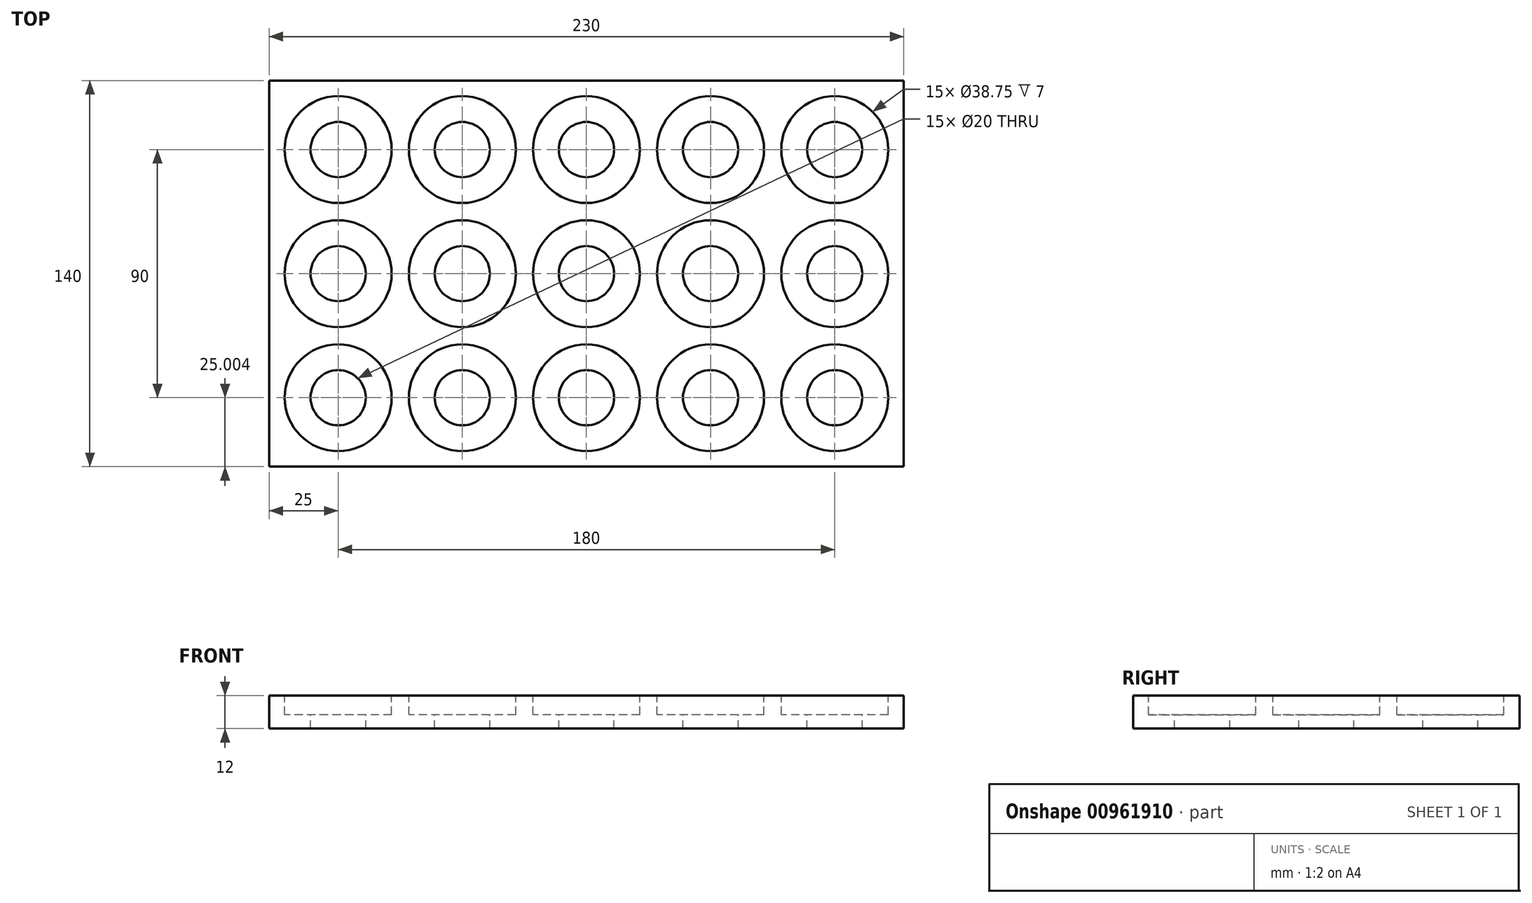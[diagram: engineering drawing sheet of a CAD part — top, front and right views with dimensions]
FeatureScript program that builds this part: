
annotation { "Feature Type Name" : "Feature", "Feature Type Description" : "" }
export const myFeature = defineFeature(function(context is Context, id is Id, definition is map)
    precondition{}
    {
        {
            var Q0;
            Q0=qCreatedBy(makeId("Top.planeOp"),FACE);
            var sketch = newSketch(context, id + "F0", { "sketchPlane" : qUnion([Q0])});
            skLineSegment(sketch, "E0.bottom", {"start": v(-57.94, 101.27) * mm, "end": v(172.06, 101.27) * mm});
            skLineSegment(sketch, "E0.top", {"start": v(-57.94, -38.73) * mm, "end": v(172.06, -38.73) * mm});
            skLineSegment(sketch, "E0.left", {"start": v(-57.94, 101.27) * mm, "end": v(-57.94, -38.73) * mm});
            skLineSegment(sketch, "E0.right", {"start": v(172.06, 101.27) * mm, "end": v(172.06, -38.73) * mm});
            skSolve(sketch);
        }
        {
            var Q0;
            Q0=qSketchRegion(id+"F0",true);
            extrude(context, id + "F1", {"entities" : qUnion([Q0]), "depth" : 12 * mm, "offsetDistance" : 25 * mm});
        }
        {
            var Q0;
            Q0=makeQuery(id+"F1.opExtrude","CAP_FACE",FACE,{"disambiguationData":[OSD([sQuery(id+"F0.wireOp",EDGE,"E0.bottom"),sQuery(id+"F0.wireOp",EDGE,"E0.top"),sQuery(id+"F0.wireOp",EDGE,"E0.left"),sQuery(id+"F0.wireOp",EDGE,"E0.right")])],"isStart":false});
            var sketch = newSketch(context, id + "F2", { "sketchPlane" : qUnion([Q0])});
            skCircle(sketch, "E1", {"center": v(-32.94, 76.27) * mm, "radius": 19.38 * mm});
            skCircle(sketch, "E2", {"center": v(-32.94, 31.27) * mm, "radius": 19.38 * mm});
            skPoint(sketch, "E2.centerSnap0", {"position": v(-57.94, 31.27) * mm});
            skCircle(sketch, "E3", {"center": v(-32.94, -13.73) * mm, "radius": 19.38 * mm});
            skCircle(sketch, "E4", {"center": v(12.06, 76.27) * mm, "radius": 19.38 * mm});
            skCircle(sketch, "E5", {"center": v(12.06, 31.27) * mm, "radius": 19.38 * mm});
            skCircle(sketch, "E6", {"center": v(12.06, -13.73) * mm, "radius": 19.38 * mm});
            skCircle(sketch, "E7", {"center": v(57.06, 76.27) * mm, "radius": 19.38 * mm});
            skCircle(sketch, "E8", {"center": v(57.06, 31.27) * mm, "radius": 19.38 * mm});
            skCircle(sketch, "E9", {"center": v(57.06, -13.73) * mm, "radius": 19.38 * mm});
            skCircle(sketch, "E10", {"center": v(102.06, 76.27) * mm, "radius": 19.38 * mm});
            skCircle(sketch, "E11", {"center": v(102.06, 31.27) * mm, "radius": 19.38 * mm});
            skCircle(sketch, "E12", {"center": v(102.06, -13.73) * mm, "radius": 19.38 * mm});
            skCircle(sketch, "E13", {"center": v(147.06, 76.27) * mm, "radius": 19.38 * mm});
            skCircle(sketch, "E14", {"center": v(147.06, 31.27) * mm, "radius": 19.38 * mm});
            skCircle(sketch, "E15", {"center": v(147.06, -13.73) * mm, "radius": 19.38 * mm});
            skCircle(sketch, "E16", {"center": v(-32.94, 76.27) * mm, "radius": 10 * mm});
            skCircle(sketch, "E17", {"center": v(-32.94, 31.27) * mm, "radius": 10 * mm});
            skCircle(sketch, "E18", {"center": v(-32.94, -13.73) * mm, "radius": 10 * mm});
            skCircle(sketch, "E19", {"center": v(12.06, -13.73) * mm, "radius": 10 * mm});
            skCircle(sketch, "E20", {"center": v(12.06, 31.27) * mm, "radius": 10 * mm});
            skCircle(sketch, "E21", {"center": v(12.06, 76.27) * mm, "radius": 10 * mm});
            skCircle(sketch, "E22", {"center": v(57.06, 76.27) * mm, "radius": 10 * mm});
            skCircle(sketch, "E23", {"center": v(57.06, 31.27) * mm, "radius": 10 * mm});
            skCircle(sketch, "E24", {"center": v(57.06, -13.73) * mm, "radius": 10 * mm});
            skCircle(sketch, "E25", {"center": v(102.06, -13.73) * mm, "radius": 10 * mm});
            skCircle(sketch, "E26", {"center": v(147.06, -13.73) * mm, "radius": 10 * mm});
            skCircle(sketch, "E27", {"center": v(147.06, 31.27) * mm, "radius": 10 * mm});
            skCircle(sketch, "E28", {"center": v(102.06, 31.27) * mm, "radius": 10 * mm});
            skCircle(sketch, "E29", {"center": v(102.06, 76.27) * mm, "radius": 10 * mm});
            skCircle(sketch, "E30", {"center": v(147.06, 76.27) * mm, "radius": 10 * mm});
            skPoint(sketch, "E31", {"position": v(-8.35, 52.35) * mm});
            skSolve(sketch);
        }
        {
            var Q0;
            Q0=makeQuery(id+"F2.imprint","IMPRINT",FACE,{"disambiguationData":[TD([[makeQuery(id+"F2.imprint","IMPRINT",EDGE,{"derivedFrom":sQuery(id+"F2.wireOp",EDGE,"E1")}),1.0]])]});
            var Q1;
            Q1=makeQuery(id+"F2.imprint","IMPRINT",FACE,{"disambiguationData":[TD([[makeQuery(id+"F2.imprint","IMPRINT",EDGE,{"derivedFrom":sQuery(id+"F2.wireOp",EDGE,"E2")}),1.0]])]});
            var Q2;
            Q2=makeQuery(id+"F2.imprint","IMPRINT",FACE,{"disambiguationData":[TD([[makeQuery(id+"F2.imprint","IMPRINT",EDGE,{"derivedFrom":sQuery(id+"F2.wireOp",EDGE,"E3")}),1.0]])]});
            var Q3;
            Q3=makeQuery(id+"F2.imprint","IMPRINT",FACE,{"disambiguationData":[TD([[makeQuery(id+"F2.imprint","IMPRINT",EDGE,{"derivedFrom":sQuery(id+"F2.wireOp",EDGE,"E6")}),1.0]])]});
            var Q4;
            Q4=makeQuery(id+"F2.imprint","IMPRINT",FACE,{"disambiguationData":[TD([[makeQuery(id+"F2.imprint","IMPRINT",EDGE,{"derivedFrom":sQuery(id+"F2.wireOp",EDGE,"E5")}),1.0]])]});
            var Q5;
            Q5=makeQuery(id+"F2.imprint","IMPRINT",FACE,{"disambiguationData":[TD([[makeQuery(id+"F2.imprint","IMPRINT",EDGE,{"derivedFrom":sQuery(id+"F2.wireOp",EDGE,"E4")}),1.0]])]});
            var Q6;
            Q6=makeQuery(id+"F2.imprint","IMPRINT",FACE,{"disambiguationData":[TD([[makeQuery(id+"F2.imprint","IMPRINT",EDGE,{"derivedFrom":sQuery(id+"F2.wireOp",EDGE,"E7")}),1.0]])]});
            var Q7;
            Q7=makeQuery(id+"F2.imprint","IMPRINT",FACE,{"disambiguationData":[TD([[makeQuery(id+"F2.imprint","IMPRINT",EDGE,{"derivedFrom":sQuery(id+"F2.wireOp",EDGE,"E8")}),1.0]])]});
            var Q8;
            Q8=makeQuery(id+"F2.imprint","IMPRINT",FACE,{"disambiguationData":[TD([[makeQuery(id+"F2.imprint","IMPRINT",EDGE,{"derivedFrom":sQuery(id+"F2.wireOp",EDGE,"E9")}),1.0]])]});
            var Q9;
            Q9=makeQuery(id+"F2.imprint","IMPRINT",FACE,{"disambiguationData":[TD([[makeQuery(id+"F2.imprint","IMPRINT",EDGE,{"derivedFrom":sQuery(id+"F2.wireOp",EDGE,"E12")}),1.0]])]});
            var Q10;
            Q10=makeQuery(id+"F2.imprint","IMPRINT",FACE,{"disambiguationData":[TD([[makeQuery(id+"F2.imprint","IMPRINT",EDGE,{"derivedFrom":sQuery(id+"F2.wireOp",EDGE,"E11")}),1.0]])]});
            var Q11;
            Q11=makeQuery(id+"F2.imprint","IMPRINT",FACE,{"disambiguationData":[TD([[makeQuery(id+"F2.imprint","IMPRINT",EDGE,{"derivedFrom":sQuery(id+"F2.wireOp",EDGE,"E10")}),1.0]])]});
            var Q12;
            Q12=makeQuery(id+"F2.imprint","IMPRINT",FACE,{"disambiguationData":[TD([[makeQuery(id+"F2.imprint","IMPRINT",EDGE,{"derivedFrom":sQuery(id+"F2.wireOp",EDGE,"E13")}),1.0]])]});
            var Q13;
            Q13=makeQuery(id+"F2.imprint","IMPRINT",FACE,{"disambiguationData":[TD([[makeQuery(id+"F2.imprint","IMPRINT",EDGE,{"derivedFrom":sQuery(id+"F2.wireOp",EDGE,"E14")}),1.0]])]});
            var Q14;
            Q14=makeQuery(id+"F2.imprint","IMPRINT",FACE,{"disambiguationData":[TD([[makeQuery(id+"F2.imprint","IMPRINT",EDGE,{"derivedFrom":sQuery(id+"F2.wireOp",EDGE,"E15")}),1.0]])]});
            extrude(context, id + "F3", {"entities" : qUnion([Q0, Q1, Q2, Q3, Q4, Q5, Q6, Q7, Q8, Q9, Q10, Q11, Q12, Q13, Q14]), "operationType" : NewBodyOperationType.REMOVE, "oppositeDirection" : true, "depth" : 7 * mm, "offsetDistance" : 25 * mm});
        }
        {
            var Q0;
            Q0=makeQuery(id+"F3.boolean.opBoolean","SPLIT",FACE,{"disambiguationData":[TD([makeQuery(id+"F3.opExtrude","SWEPT_FACE",FACE,{"disambiguationData":[OSD([sQuery(id+"F2.wireOp",EDGE,"E16")])]})])],"derivedFrom":makeQuery(id+"F1.opExtrude","CAP_FACE",FACE,{"disambiguationData":[OSD([sQuery(id+"F0.wireOp",EDGE,"E0.bottom"),sQuery(id+"F0.wireOp",EDGE,"E0.top"),sQuery(id+"F0.wireOp",EDGE,"E0.left"),sQuery(id+"F0.wireOp",EDGE,"E0.right")])],"isStart":false})});
            var Q1;
            Q1=makeQuery(id+"F3.boolean.opBoolean","SPLIT",FACE,{"disambiguationData":[TD([makeQuery(id+"F3.opExtrude","SWEPT_FACE",FACE,{"disambiguationData":[OSD([sQuery(id+"F2.wireOp",EDGE,"E21")])]})])],"derivedFrom":makeQuery(id+"F1.opExtrude","CAP_FACE",FACE,{"disambiguationData":[OSD([sQuery(id+"F0.wireOp",EDGE,"E0.bottom"),sQuery(id+"F0.wireOp",EDGE,"E0.top"),sQuery(id+"F0.wireOp",EDGE,"E0.left"),sQuery(id+"F0.wireOp",EDGE,"E0.right")])],"isStart":false})});
            var Q2;
            Q2=makeQuery(id+"F3.boolean.opBoolean","SPLIT",FACE,{"disambiguationData":[TD([makeQuery(id+"F3.opExtrude","SWEPT_FACE",FACE,{"disambiguationData":[OSD([sQuery(id+"F2.wireOp",EDGE,"E22")])]})])],"derivedFrom":makeQuery(id+"F1.opExtrude","CAP_FACE",FACE,{"disambiguationData":[OSD([sQuery(id+"F0.wireOp",EDGE,"E0.bottom"),sQuery(id+"F0.wireOp",EDGE,"E0.top"),sQuery(id+"F0.wireOp",EDGE,"E0.left"),sQuery(id+"F0.wireOp",EDGE,"E0.right")])],"isStart":false})});
            var Q3;
            Q3=makeQuery(id+"F3.boolean.opBoolean","SPLIT",FACE,{"disambiguationData":[TD([makeQuery(id+"F3.opExtrude","SWEPT_FACE",FACE,{"disambiguationData":[OSD([sQuery(id+"F2.wireOp",EDGE,"E29")])]})])],"derivedFrom":makeQuery(id+"F1.opExtrude","CAP_FACE",FACE,{"disambiguationData":[OSD([sQuery(id+"F0.wireOp",EDGE,"E0.bottom"),sQuery(id+"F0.wireOp",EDGE,"E0.top"),sQuery(id+"F0.wireOp",EDGE,"E0.left"),sQuery(id+"F0.wireOp",EDGE,"E0.right")])],"isStart":false})});
            var Q4;
            Q4=makeQuery(id+"F3.boolean.opBoolean","SPLIT",FACE,{"disambiguationData":[TD([makeQuery(id+"F3.opExtrude","SWEPT_FACE",FACE,{"disambiguationData":[OSD([sQuery(id+"F2.wireOp",EDGE,"E30")])]})])],"derivedFrom":makeQuery(id+"F1.opExtrude","CAP_FACE",FACE,{"disambiguationData":[OSD([sQuery(id+"F0.wireOp",EDGE,"E0.bottom"),sQuery(id+"F0.wireOp",EDGE,"E0.top"),sQuery(id+"F0.wireOp",EDGE,"E0.left"),sQuery(id+"F0.wireOp",EDGE,"E0.right")])],"isStart":false})});
            var Q5;
            Q5=makeQuery(id+"F3.boolean.opBoolean","SPLIT",FACE,{"disambiguationData":[TD([makeQuery(id+"F3.opExtrude","SWEPT_FACE",FACE,{"disambiguationData":[OSD([sQuery(id+"F2.wireOp",EDGE,"E27")])]})])],"derivedFrom":makeQuery(id+"F1.opExtrude","CAP_FACE",FACE,{"disambiguationData":[OSD([sQuery(id+"F0.wireOp",EDGE,"E0.bottom"),sQuery(id+"F0.wireOp",EDGE,"E0.top"),sQuery(id+"F0.wireOp",EDGE,"E0.left"),sQuery(id+"F0.wireOp",EDGE,"E0.right")])],"isStart":false})});
            var Q6;
            Q6=makeQuery(id+"F3.boolean.opBoolean","SPLIT",FACE,{"disambiguationData":[TD([makeQuery(id+"F3.opExtrude","SWEPT_FACE",FACE,{"disambiguationData":[OSD([sQuery(id+"F2.wireOp",EDGE,"E28")])]})])],"derivedFrom":makeQuery(id+"F1.opExtrude","CAP_FACE",FACE,{"disambiguationData":[OSD([sQuery(id+"F0.wireOp",EDGE,"E0.bottom"),sQuery(id+"F0.wireOp",EDGE,"E0.top"),sQuery(id+"F0.wireOp",EDGE,"E0.left"),sQuery(id+"F0.wireOp",EDGE,"E0.right")])],"isStart":false})});
            var Q7;
            Q7=makeQuery(id+"F3.boolean.opBoolean","SPLIT",FACE,{"disambiguationData":[TD([makeQuery(id+"F3.opExtrude","SWEPT_FACE",FACE,{"disambiguationData":[OSD([sQuery(id+"F2.wireOp",EDGE,"E23")])]})])],"derivedFrom":makeQuery(id+"F1.opExtrude","CAP_FACE",FACE,{"disambiguationData":[OSD([sQuery(id+"F0.wireOp",EDGE,"E0.bottom"),sQuery(id+"F0.wireOp",EDGE,"E0.top"),sQuery(id+"F0.wireOp",EDGE,"E0.left"),sQuery(id+"F0.wireOp",EDGE,"E0.right")])],"isStart":false})});
            var Q8;
            Q8=makeQuery(id+"F3.boolean.opBoolean","SPLIT",FACE,{"disambiguationData":[TD([makeQuery(id+"F3.opExtrude","SWEPT_FACE",FACE,{"disambiguationData":[OSD([sQuery(id+"F2.wireOp",EDGE,"E20")])]})])],"derivedFrom":makeQuery(id+"F1.opExtrude","CAP_FACE",FACE,{"disambiguationData":[OSD([sQuery(id+"F0.wireOp",EDGE,"E0.bottom"),sQuery(id+"F0.wireOp",EDGE,"E0.top"),sQuery(id+"F0.wireOp",EDGE,"E0.left"),sQuery(id+"F0.wireOp",EDGE,"E0.right")])],"isStart":false})});
            var Q9;
            Q9=makeQuery(id+"F3.boolean.opBoolean","SPLIT",FACE,{"disambiguationData":[TD([makeQuery(id+"F3.opExtrude","SWEPT_FACE",FACE,{"disambiguationData":[OSD([sQuery(id+"F2.wireOp",EDGE,"E17")])]})])],"derivedFrom":makeQuery(id+"F1.opExtrude","CAP_FACE",FACE,{"disambiguationData":[OSD([sQuery(id+"F0.wireOp",EDGE,"E0.bottom"),sQuery(id+"F0.wireOp",EDGE,"E0.top"),sQuery(id+"F0.wireOp",EDGE,"E0.left"),sQuery(id+"F0.wireOp",EDGE,"E0.right")])],"isStart":false})});
            var Q10;
            Q10=makeQuery(id+"F3.boolean.opBoolean","SPLIT",FACE,{"disambiguationData":[TD([makeQuery(id+"F3.opExtrude","SWEPT_FACE",FACE,{"disambiguationData":[OSD([sQuery(id+"F2.wireOp",EDGE,"E18")])]})])],"derivedFrom":makeQuery(id+"F1.opExtrude","CAP_FACE",FACE,{"disambiguationData":[OSD([sQuery(id+"F0.wireOp",EDGE,"E0.bottom"),sQuery(id+"F0.wireOp",EDGE,"E0.top"),sQuery(id+"F0.wireOp",EDGE,"E0.left"),sQuery(id+"F0.wireOp",EDGE,"E0.right")])],"isStart":false})});
            var Q11;
            Q11=makeQuery(id+"F3.boolean.opBoolean","SPLIT",FACE,{"disambiguationData":[TD([makeQuery(id+"F3.opExtrude","SWEPT_FACE",FACE,{"disambiguationData":[OSD([sQuery(id+"F2.wireOp",EDGE,"E19")])]})])],"derivedFrom":makeQuery(id+"F1.opExtrude","CAP_FACE",FACE,{"disambiguationData":[OSD([sQuery(id+"F0.wireOp",EDGE,"E0.bottom"),sQuery(id+"F0.wireOp",EDGE,"E0.top"),sQuery(id+"F0.wireOp",EDGE,"E0.left"),sQuery(id+"F0.wireOp",EDGE,"E0.right")])],"isStart":false})});
            var Q12;
            Q12=makeQuery(id+"F3.boolean.opBoolean","SPLIT",FACE,{"disambiguationData":[TD([makeQuery(id+"F3.opExtrude","SWEPT_FACE",FACE,{"disambiguationData":[OSD([sQuery(id+"F2.wireOp",EDGE,"E24")])]})])],"derivedFrom":makeQuery(id+"F1.opExtrude","CAP_FACE",FACE,{"disambiguationData":[OSD([sQuery(id+"F0.wireOp",EDGE,"E0.bottom"),sQuery(id+"F0.wireOp",EDGE,"E0.top"),sQuery(id+"F0.wireOp",EDGE,"E0.left"),sQuery(id+"F0.wireOp",EDGE,"E0.right")])],"isStart":false})});
            var Q13;
            Q13=makeQuery(id+"F3.boolean.opBoolean","SPLIT",FACE,{"disambiguationData":[TD([makeQuery(id+"F3.opExtrude","SWEPT_FACE",FACE,{"disambiguationData":[OSD([sQuery(id+"F2.wireOp",EDGE,"E25")])]})])],"derivedFrom":makeQuery(id+"F1.opExtrude","CAP_FACE",FACE,{"disambiguationData":[OSD([sQuery(id+"F0.wireOp",EDGE,"E0.bottom"),sQuery(id+"F0.wireOp",EDGE,"E0.top"),sQuery(id+"F0.wireOp",EDGE,"E0.left"),sQuery(id+"F0.wireOp",EDGE,"E0.right")])],"isStart":false})});
            var Q14;
            Q14=makeQuery(id+"F3.boolean.opBoolean","SPLIT",FACE,{"disambiguationData":[TD([makeQuery(id+"F3.opExtrude","SWEPT_FACE",FACE,{"disambiguationData":[OSD([sQuery(id+"F2.wireOp",EDGE,"E26")])]})])],"derivedFrom":makeQuery(id+"F1.opExtrude","CAP_FACE",FACE,{"disambiguationData":[OSD([sQuery(id+"F0.wireOp",EDGE,"E0.bottom"),sQuery(id+"F0.wireOp",EDGE,"E0.top"),sQuery(id+"F0.wireOp",EDGE,"E0.left"),sQuery(id+"F0.wireOp",EDGE,"E0.right")])],"isStart":false})});
            extrude(context, id + "F4", {"entities" : qUnion([Q0, Q1, Q2, Q3, Q4, Q5, Q6, Q7, Q8, Q9, Q10, Q11, Q12, Q13, Q14]), "operationType" : NewBodyOperationType.REMOVE, "oppositeDirection" : true, "depth" : 25 * mm, "offsetDistance" : 25 * mm});
        }
    });
